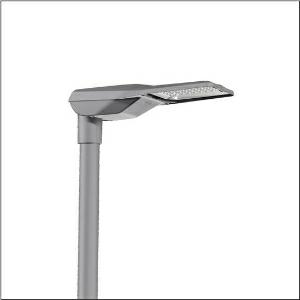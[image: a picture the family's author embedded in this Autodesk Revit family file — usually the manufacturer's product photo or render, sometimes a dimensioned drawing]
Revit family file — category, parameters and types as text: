
# Revit family: streetlight_sl_21_iq_mini___st0_5a_5xe2b41g08gb_465e
name_source: partatom
category: Lighting Fixtures
units: mm (PartAtom-declared; Revit-internal decimal feet)

## family parameters
Cut with Voids When Loaded = No
Host = Face
Light Source = No
Part Type = Normal
Room Calculation Point = No
Round Connector Dimension = Use Diameter
Shared = No

## types (1)
- --- (1 x LED, 5920 lm, 37.1 W, 4000K)
    Apparent Load = 37 VA
    CIE Flux Codes = 41 75 97 100 100
    Color Rendering = 70
    Color Temperature = 4000K
    Default Elevation = 1800 mm
    Description = Streetlight SL 21 mini, mast luminaire, primary light control with lens, of PMMA, primary optical cover: cover, of toughened safety glass, transparent, light distribution: ST0.5a, light emission: direct distribution, primary light characteristic: asymmetric, installation type: post-top, side-entry, LED, High Power LED, rated luminous flux: 5.920lm, luminous efficacy: 160lm/W, light colour: 740, colour temperature: 4000K, control gear: ECG iQ, control: Street-Remote, Auto-Match, Temp-Guard, Lumen-Switch, Night-Set, Smart-Wire, Light-Fading, Desk-Remote (wireless, voltage-free reading and setting of iQ features in the workshop via application-optimized NFC function/RFID function), optimised constant luminous flux control (CLO 2.0), mains connection: 220..240V, AC, 50/60Hz, start of lifetime: 37W, end of lifetime: 39W, reduction: 18W, luminaire housing, of diecast aluminium, powder-coated, Siteco® metallic grey (DB 702S), corrosivity category C5 according to DIN EN ISO 12944, length: 628mm, width: 235mm, height: 110mm, spigot size: 60/76mm (post-top) and 42/60/76mm (side-entry), mast flange for spigot size: 42mm: 5XC10008XM4, 60mm: 5XC10008XM2, 76/60mm: 5XC10108XM1, protection rating (complete): IP66, insulation class (complete): insulation class II (safety insulation), certification: CE, ENEC, VDE, impact resistance: IK09, permissible operating ambient temperature for outdoor applications: -40..+50°C, standard-compliant lighting for roads and squares, packaging unit: 1 piece

Light Distribution: ST0.5a
    Height = 110 mm
    Lamp = 1 x LED
    Lamp Light Flux = 5920 lm
    Lamp Power = 37.1 W
    Lamp count = 1
    Length = 625 mm
    Luminous efficacy = 160 lm/W
    Manufacturer = Siteco
    ModVariant = No
    Model = 5XE2B41G08GB
    Number of Poles = 1
    OnlyDefault = Yes
    Power Factor = 1
    Product Name = Streetlight SL 21 iQ mini | ST0.5a
    Product group = mast luminaire | pylon top
    ProductGroupID = 6100
    Protection Class = Protection class II
    Protection Degree = IP 66
    RLX_Detail_Level = 1
    RlxData = <blob elided: 103289 chars, md5=70f0add9>
    Socket = socket
    Standby Power = 0 W
    System Light Flux = 5920 lm
    System Power = 37 W
    Type Comments = factory setting: luminous flux: 100 % | dim-lin: 254 | 385 mA
    Type Image = l_1003519.jpg
    URL = http://relux.com
    VarID = @adj_111263
    Voltage = 0 V
    Weight = 0.00 kg
    Width = 234 mm

## geometry (parser evidence)
native form markers: Blend x4, Sweep x11
no freeform markers — native parametric forms only
